# Revit family: ITK_Проходной адаптер категории 5E_Keystone Jack_Неэкранированный
name_source: partatom
category: Обобщенные модели
units: mm (PartAtom-declared; Revit-internal decimal feet)

## family parameters
Всегда вертикально = Да
Может служить основой для арматурных стержней = Нет
На основе рабочей плоскости = Нет
Общий = Нет
При загрузке вырезать с полостями = Нет
Размер круглого соединителя = Использовать диаметр
Тип детали = Нормальный
Точка расчета площади = Нет

## types (1)
- CS7-1C5EU
    ADSK_URL страницы изделия = https://www.itk-group.ru
    ADSK_Версия Revit = 2019
    ADSK_Версия семейства = 1.0
    ADSK_Группирование = I. ЩИТЫ И ПУЛЬТЫ
    ADSK_Единица измерения = шт
    ADSK_Завод-изготовитель = IEK
    ADSK_Код изделия = CS7-1C5EU
    ADSK_Масса = 0
    ADSK_Материал наименование = Пластик
    ADSK_Наименование = ITK Проходной адаптер кат.5E UTP, RJ45-RJ45, тип Keystone Jack
    IEK_URL = https://www.itk-group.ru
    IEK_Описание = Соответствие международным стандартам качества, что обеспечивает совместимость с компонентами и с кабелем.
Изготовлены из высококачественных негорючих материалов и отличаются надежностью и удобством эксплуатации.
    IEK_Цена за единицу = 106.9
    KSI_CMa_Строительные материалы = 01.7.14.03
    KSI_CPr_Строительные изделия = 61.1.03.04
    URL = https://www.iek.ru
    Высота = 16 мм
    Глубина = 27 мм
    Изготовитель = ITK
    Материал = Пластик белый
    Ширина = 15 мм
